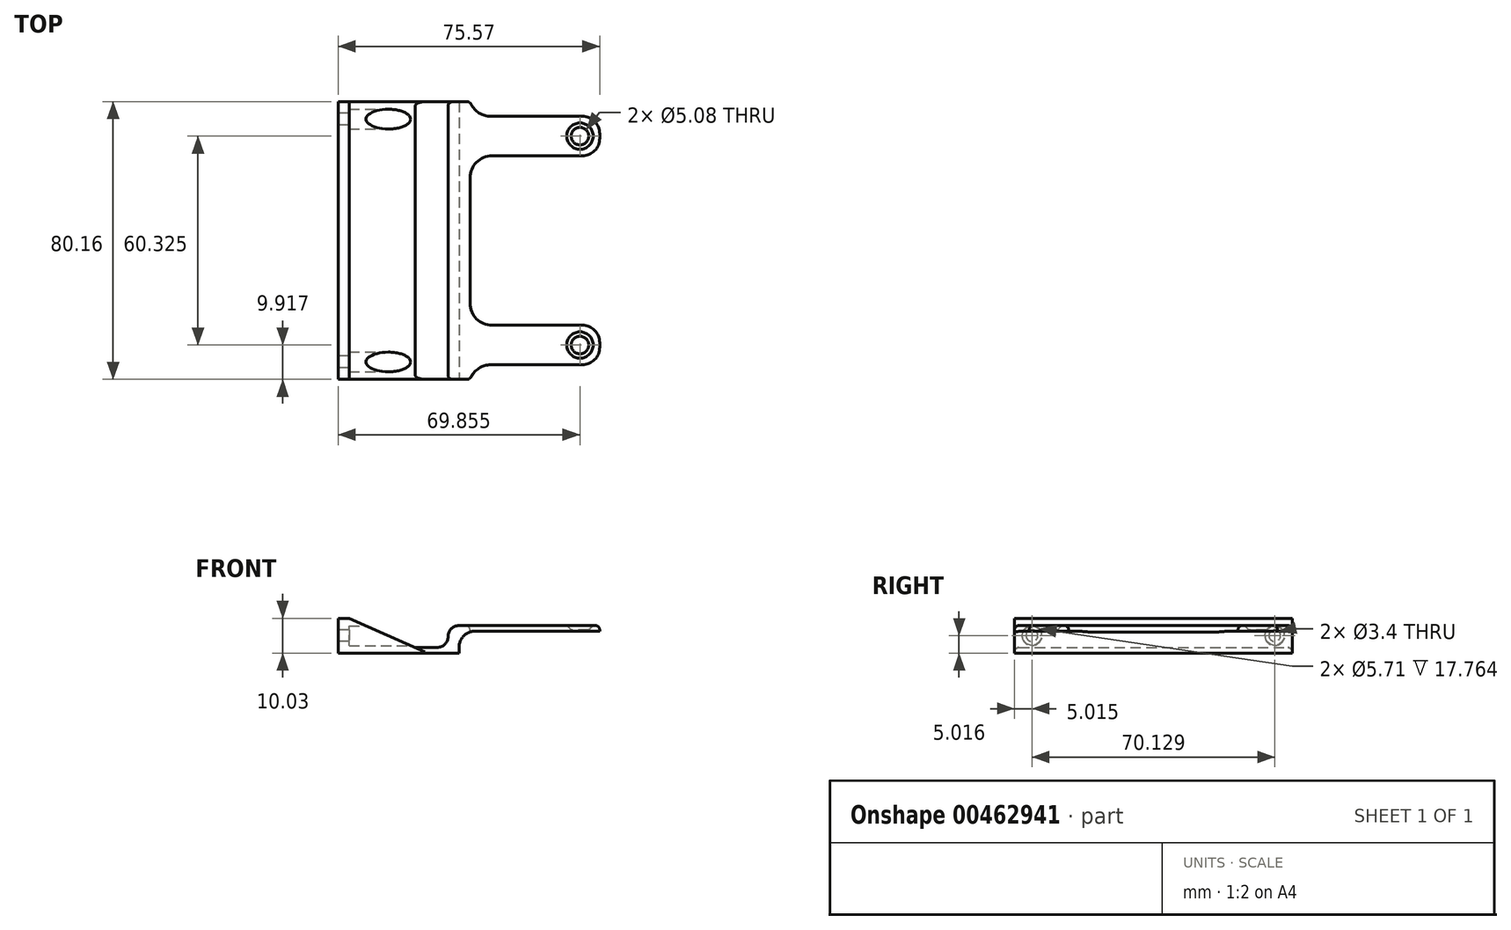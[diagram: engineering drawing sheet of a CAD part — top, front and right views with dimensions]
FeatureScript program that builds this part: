
annotation { "Feature Type Name" : "Feature", "Feature Type Description" : "" }
export const myFeature = defineFeature(function(context is Context, id is Id, definition is map)
    precondition{}
    {
        {
            var Q0;
            Q0=qCreatedBy(makeId("Top.planeOp"),FACE);
            var sketch = newSketch(context, id + "F0", { "sketchPlane" : qUnion([Q0])});
            skLineSegment(sketch, "E0.bottom", {"start": v(-34.93, 40.08) * mm, "end": v(0, 40.08) * mm});
            skLineSegment(sketch, "E0.top", {"start": v(-34.93, -40.08) * mm, "end": v(0, -40.08) * mm});
            skLineSegment(sketch, "E0.left", {"start": v(-34.93, 40.08) * mm, "end": v(-34.93, -40.08) * mm});
            skLineSegment(sketch, "E0.right", {"start": v(0, 40.08) * mm, "end": v(0, -40.08) * mm});
            skSolve(sketch);
        }
        {
            var Q0;
            Q0 = qSketchRegion(id + "F0", true);
            extrude(context, id + "F1", {"entities" : qUnion([Q0]), "depth" : 1.59 * mm});
        }
        {
            var Q0;
            Q0=qCreatedBy(makeId("Top.planeOp"),FACE);
            var sketch = newSketch(context, id + "F2", { "sketchPlane" : qUnion([Q0])});
            skLineSegment(sketch, "E1.bottom", {"start": v(0, 40.08) * mm, "end": v(-3.18, 40.08) * mm});
            skLineSegment(sketch, "E1.top", {"start": v(0, -40.08) * mm, "end": v(-3.17, -40.08) * mm});
            skLineSegment(sketch, "E1.left", {"start": v(0, 40.08) * mm, "end": v(0, -40.08) * mm});
            skLineSegment(sketch, "E1.right", {"start": v(-3.18, 40.08) * mm, "end": v(-3.17, -40.08) * mm});
            skSolve(sketch);
        }
        {
            var Q0;
            Q0 = qSketchRegion(id + "F2", true);
            extrude(context, id + "F3", {"entities" : qUnion([Q0]), "operationType" : NewBodyOperationType.ADD, "depth" : 6.35 * mm});
        }
        {
            var Q0;
            Q0=makeQuery(id+"F3.opExtrude","CAP_FACE",FACE,{"disambiguationData":[OSD([sQuery(id+"F2.wireOp",EDGE,"E1.bottom"),sQuery(id+"F2.wireOp",EDGE,"E1.top"),sQuery(id+"F2.wireOp",EDGE,"E1.left"),sQuery(id+"F2.wireOp",EDGE,"E1.right")])],"isStart":false});
            var sketch = newSketch(context, id + "F4", { "sketchPlane" : qUnion([Q0])});
            skLineSegment(sketch, "E2", {"start": v(0, 0) * mm, "end": v(-34.93, 0) * mm, "construction": true});
            skPoint(sketch, "E2.endSnap0", {"position": v(0, 0) * mm});
            skLineSegment(sketch, "E3.bottom", {"start": v(-3.18, 35.88) * mm, "end": v(40.64, 35.88) * mm});
            skLineSegment(sketch, "E3.top", {"start": v(-3.18, 24.45) * mm, "end": v(40.64, 24.45) * mm});
            skLineSegment(sketch, "E3.left", {"start": v(-3.18, 35.88) * mm, "end": v(-3.18, 24.45) * mm});
            skLineSegment(sketch, "E3.right", {"start": v(40.64, 35.88) * mm, "end": v(40.64, 24.45) * mm});
            skLineSegment(sketch, "E4", {"start": v(34.92, 35.88) * mm, "end": v(34.92, 30.16) * mm, "construction": true});
            skLineSegment(sketch, "E5", {"start": v(34.93, 30.16) * mm, "end": v(34.93, 24.45) * mm, "construction": true});
            skLineSegment(sketch, "E6", {"start": v(34.93, 30.16) * mm, "end": v(40.64, 30.16) * mm, "construction": true});
            skCircle(sketch, "E7", {"center": v(34.93, 30.16) * mm, "radius": 2.54 * mm});
            skLineSegment(sketch, "E8.MirrorCS", {"start": v(-3.18, -35.88) * mm, "end": v(40.64, -35.88) * mm});
            skLineSegment(sketch, "E9.MirrorCS", {"start": v(34.93, -30.16) * mm, "end": v(40.64, -30.16) * mm, "construction": true});
            skLineSegment(sketch, "E10.MirrorCS", {"start": v(-3.18, -24.45) * mm, "end": v(40.64, -24.45) * mm});
            skLineSegment(sketch, "E11.MirrorCS", {"start": v(-3.18, -35.88) * mm, "end": v(-3.18, -24.45) * mm});
            skCircle(sketch, "E12.MirrorC", {"center": v(34.93, -30.16) * mm, "radius": 2.54 * mm});
            skLineSegment(sketch, "E13.MirrorCS", {"start": v(40.64, -35.88) * mm, "end": v(40.64, -24.45) * mm});
            skLineSegment(sketch, "E14.MirrorCS", {"start": v(34.93, -30.16) * mm, "end": v(34.93, -24.45) * mm, "construction": true});
            skLineSegment(sketch, "E15.MirrorCS", {"start": v(34.93, -35.88) * mm, "end": v(34.93, -30.16) * mm, "construction": true});
            skSolve(sketch);
        }
        {
            var Q0;
            Q0 = qSketchRegion(id + "F4", true);
            extrude(context, id + "F5", {"entities" : qUnion([Q0]), "operationType" : NewBodyOperationType.ADD, "depth" : 1.59 * mm});
        }
        {
            var Q0;
            Q0=makeQuery(id+"F5.opExtrude","CAP_FACE",FACE,{"disambiguationData":[OSD([sQuery(id+"F4.wireOp",EDGE,"E3.bottom"),sQuery(id+"F4.wireOp",EDGE,"E3.top"),sQuery(id+"F4.wireOp",EDGE,"E3.left"),sQuery(id+"F4.wireOp",EDGE,"E3.right"),sQuery(id+"F4.wireOp",EDGE,"E7")])],"isStart":false});
            var sketch = newSketch(context, id + "F6", { "sketchPlane" : qUnion([Q0])});
            skLineSegment(sketch, "E16.bottom", {"start": v(-3.18, 40.08) * mm, "end": v(3.17, 40.08) * mm});
            skLineSegment(sketch, "E16.top", {"start": v(-3.17, -40.08) * mm, "end": v(3.17, -40.08) * mm});
            skLineSegment(sketch, "E16.left", {"start": v(-3.18, 40.08) * mm, "end": v(-3.18, -40.08) * mm});
            skLineSegment(sketch, "E16.right", {"start": v(3.17, 40.08) * mm, "end": v(3.17, -40.08) * mm});
            skSolve(sketch);
        }
        {
            var Q0;
            Q0 = qSketchRegion(id + "F6", true);
            var Q1;
            {var subQ1=sQuery(id+"F4.wireOp",EDGE,"E3.top");var subQ2=sQuery(id+"F2.wireOp",EDGE,"E1.right");var subQ4=sQuery(id+"F2.wireOp",EDGE,"E1.left");Q1=makeQuery(id+"F5.boolean.opBoolean","SPLIT",FACE,{"disambiguationData":[TD([makeQuery(id+"F5.opExtrude","SWEPT_FACE",FACE,{"disambiguationData":[OSD([subQ1])]})])],"derivedFrom":makeQuery(id+"F3.opExtrude","CAP_FACE",FACE,{"disambiguationData":[OSD([sQuery(id+"F2.wireOp",EDGE,"E1.bottom"),sQuery(id+"F2.wireOp",EDGE,"E1.top"),subQ4,subQ2])],"isStart":false})});}
            extrude(context, id + "F7", {"entities" : qUnion([Q0]), "operationType" : NewBodyOperationType.ADD, "endBound" : BoundingType.UP_TO_SURFACE, "oppositeDirection" : true, "endBoundEntityFace" : qUnion([Q1]), "depth" : 25.4 * mm});
        }
        {
            var Q0;
            Q0=makeQuery(id+"F5.opExtrude","SWEPT_EDGE",EDGE,{"disambiguationData":[OSD([sQuery(id+"F4.wireOp",EDGE,"E8.MirrorCS"),sQuery(id+"F4.wireOp",EDGE,"E13.MirrorCS")])]});
            var Q1;
            Q1=makeQuery(id+"F5.opExtrude","SWEPT_EDGE",EDGE,{"disambiguationData":[OSD([sQuery(id+"F4.wireOp",EDGE,"E10.MirrorCS"),sQuery(id+"F4.wireOp",EDGE,"E13.MirrorCS")])]});
            var Q2;
            Q2=makeQuery(id+"F5.opExtrude","SWEPT_EDGE",EDGE,{"disambiguationData":[OSD([sQuery(id+"F4.wireOp",EDGE,"E3.top"),sQuery(id+"F4.wireOp",EDGE,"E3.right")])]});
            var Q3;
            Q3=makeQuery(id+"F5.opExtrude","SWEPT_EDGE",EDGE,{"disambiguationData":[OSD([sQuery(id+"F4.wireOp",EDGE,"E3.bottom"),sQuery(id+"F4.wireOp",EDGE,"E3.right")])]});
            fillet(context, id + "F8", {"entities" : qUnion([Q0, Q1, Q2, Q3]), "radius" : 5.08 * mm, "tangentPropagation" : true, "allowEdgeOverflow" : false});
        }
        {
            var Q0;
            {var subQ0=sQuery(id+"F4.wireOp",EDGE,"E3.top");var subQ1=makeQuery(id+"F5.opExtrude","CAP_FACE",FACE,{"disambiguationData":[OSD([sQuery(id+"F4.wireOp",EDGE,"E3.bottom"),subQ0,sQuery(id+"F4.wireOp",EDGE,"E3.left"),sQuery(id+"F4.wireOp",EDGE,"E3.right"),sQuery(id+"F4.wireOp",EDGE,"E7")])],"isStart":true});var subQ2=sQuery(id+"F2.wireOp",EDGE,"E1.left");var subQ3=makeQuery(id+"F3.opExtrude","SWEPT_FACE",FACE,{"disambiguationData":[OSD([subQ2])]});var subQ4=makeQuery(id+"F1.opExtrude","SWEPT_FACE",FACE,{"disambiguationData":[OSD([sQuery(id+"F0.wireOp",EDGE,"E0.right")])]});var subQ5=sQuery(id+"F4.wireOp",EDGE,"E10.MirrorCS");var subQ6=makeQuery(id+"F3.opExtrude","CAP_FACE",FACE,{"disambiguationData":[OSD([sQuery(id+"F2.wireOp",EDGE,"E1.bottom"),sQuery(id+"F2.wireOp",EDGE,"E1.top"),subQ2,sQuery(id+"F2.wireOp",EDGE,"E1.right")])],"isStart":false});var subQ7=makeQuery(id+"F5.opExtrude","CAP_FACE",FACE,{"disambiguationData":[OSD([sQuery(id+"F4.wireOp",EDGE,"E8.MirrorCS"),subQ5,sQuery(id+"F4.wireOp",EDGE,"E11.MirrorCS"),sQuery(id+"F4.wireOp",EDGE,"E12.MirrorC"),sQuery(id+"F4.wireOp",EDGE,"E13.MirrorCS")])],"isStart":true});var subQ8=makeQuery(id+"F3.opExtrude","CAP_EDGE",EDGE,{"disambiguationData":[OSD([subQ2])],"isStart":false});Q0=makeQuery(id+"F7.boolean.opBoolean","MERGE",EDGE,{"derivedFrom":[makeQuery(id+"F5.boolean.opBoolean","SPLIT",EDGE,{"disambiguationData":[topologyDisambiguationEdgeConnected([subQ4,subQ3,subQ1])],"derivedFrom":subQ8}),makeQuery(id+"F5.boolean.opBoolean","SPLIT",EDGE,{"disambiguationData":[topologyDisambiguationEdgeConnected([subQ4,subQ3,subQ7])],"derivedFrom":subQ8}),makeQuery(id+"F5.boolean.opBoolean","SPLIT",EDGE,{"disambiguationData":[topologyDisambiguationEdgeConnected([subQ4,subQ6,subQ3]),TD([makeQuery(id+"F5.opExtrude","SWEPT_FACE",FACE,{"disambiguationData":[OSD([subQ0])]})])],"derivedFrom":subQ8})]});}
            fillet(context, id + "F9", {"entities" : qUnion([Q0]), "radius" : 4.76 * mm, "tangentPropagation" : true, "allowEdgeOverflow" : false});
        }
        {
            var Q0;
            Q0=makeQuery(id+"F5.opExtrude","CAP_EDGE",EDGE,{"disambiguationData":[OSD([sQuery(id+"F4.wireOp",EDGE,"E12.MirrorC")])],"isStart":false});
            var Q1;
            Q1=makeQuery(id+"F5.opExtrude","CAP_EDGE",EDGE,{"disambiguationData":[OSD([sQuery(id+"F4.wireOp",EDGE,"E7")])],"isStart":false});
            chamfer(context, id + "F10", {"entities" : qUnion([Q0, Q1]), "width" : 1.27 * mm, "tangentPropagation" : true});
        }
        {
            var Q0;
            Q0=makeQuery(id+"F1.opExtrude","SWEPT_FACE",FACE,{"disambiguationData":[OSD([sQuery(id+"F0.wireOp",EDGE,"E0.left")])]});
            var sketch = newSketch(context, id + "F11", { "sketchPlane" : qUnion([Q0])});
            skLineSegment(sketch, "E17.bottom", {"start": v(40.08, 0) * mm, "end": v(-40.08, 0) * mm});
            skLineSegment(sketch, "E17.top", {"start": v(40.08, 10.03) * mm, "end": v(-40.08, 10.03) * mm});
            skLineSegment(sketch, "E17.left", {"start": v(40.08, 0) * mm, "end": v(40.08, 10.03) * mm});
            skLineSegment(sketch, "E17.right", {"start": v(-40.08, 0) * mm, "end": v(-40.08, 10.03) * mm});
            skLineSegment(sketch, "E18", {"start": v(40.08, 5.02) * mm, "end": v(35.06, 5.02) * mm, "construction": true});
            skLineSegment(sketch, "E19", {"start": v(35.06, 5.02) * mm, "end": v(35.06, 10.03) * mm, "construction": true});
            skLineSegment(sketch, "E20", {"start": v(35.06, 5.02) * mm, "end": v(35.06, 0) * mm, "construction": true});
            skCircle(sketch, "E21", {"center": v(35.06, 5.02) * mm, "radius": 1.7 * mm});
            skCircle(sketch, "E22.MirrorC", {"center": v(-35.06, 5.02) * mm, "radius": 1.7 * mm});
            skLineSegment(sketch, "E23.MirrorCS", {"start": v(-35.06, 5.02) * mm, "end": v(-35.06, 0) * mm, "construction": true});
            skLineSegment(sketch, "E24.MirrorCS", {"start": v(-35.06, 5.02) * mm, "end": v(-35.06, 10.03) * mm, "construction": true});
            skLineSegment(sketch, "E25.MirrorCS", {"start": v(-40.08, 5.02) * mm, "end": v(-35.06, 5.02) * mm, "construction": true});
            skSolve(sketch);
        }
        {
            var Q0;
            Q0 = qSketchRegion(id + "F11", true);
            extrude(context, id + "F12", {"entities" : qUnion([Q0]), "operationType" : NewBodyOperationType.ADD, "oppositeDirection" : true, "depth" : 3.17 * mm});
        }
        {
            var Q0;
            Q0=makeQuery(id+"F12.boolean.opBoolean","MERGE",FACE,{"derivedFrom":[makeQuery(id+"F3.boolean.opBoolean","MERGE",FACE,{"derivedFrom":[makeQuery(id+"F1.opExtrude","SWEPT_FACE",FACE,{"disambiguationData":[OSD([sQuery(id+"F0.wireOp",EDGE,"E0.top")])]}),makeQuery(id+"F3.opExtrude","SWEPT_FACE",FACE,{"disambiguationData":[OSD([sQuery(id+"F2.wireOp",EDGE,"E1.top")])]})]}),makeQuery(id+"F12.opExtrude","SWEPT_FACE",FACE,{"disambiguationData":[OSD([sQuery(id+"F11.wireOp",EDGE,"E17.left")])]})]});
            var sketch = newSketch(context, id + "F13", { "sketchPlane" : qUnion([Q0])});
            skLineSegment(sketch, "E26", {"start": v(-31.75, 10.03) * mm, "end": v(-12.7, 1.59) * mm});
            skLineSegment(sketch, "E27", {"start": v(-12.7, 1.59) * mm, "end": v(-31.75, 1.59) * mm});
            skLineSegment(sketch, "E28", {"start": v(-31.75, 1.59) * mm, "end": v(-31.75, 10.03) * mm});
            skSolve(sketch);
        }
        {
            var Q0;
            Q0 = qSketchRegion(id + "F13", true);
            var Q1;
            Q1=makeQuery(id+"F12.boolean.opBoolean","MERGE",FACE,{"derivedFrom":[makeQuery(id+"F3.boolean.opBoolean","MERGE",FACE,{"derivedFrom":[makeQuery(id+"F1.opExtrude","SWEPT_FACE",FACE,{"disambiguationData":[OSD([sQuery(id+"F0.wireOp",EDGE,"E0.bottom")])]}),makeQuery(id+"F3.opExtrude","SWEPT_FACE",FACE,{"disambiguationData":[OSD([sQuery(id+"F2.wireOp",EDGE,"E1.bottom")])]})]}),makeQuery(id+"F12.opExtrude","SWEPT_FACE",FACE,{"disambiguationData":[OSD([sQuery(id+"F11.wireOp",EDGE,"E17.right")])]})]});
            extrude(context, id + "F14", {"entities" : qUnion([Q0]), "operationType" : NewBodyOperationType.ADD, "endBound" : BoundingType.UP_TO_SURFACE, "oppositeDirection" : true, "endBoundEntityFace" : qUnion([Q1]), "depth" : 25.4 * mm});
        }
        {
            var Q0;
            Q0=makeQuery(id+"F7.boolean.opBoolean","MERGE",FACE,{"derivedFrom":[makeQuery(id+"F5.boolean.opBoolean","MERGE",FACE,{"derivedFrom":[makeQuery(id+"F3.opExtrude","SWEPT_FACE",FACE,{"disambiguationData":[OSD([sQuery(id+"F2.wireOp",EDGE,"E1.right")])]}),makeQuery(id+"F5.opExtrude","SWEPT_FACE",FACE,{"disambiguationData":[OSD([sQuery(id+"F4.wireOp",EDGE,"E3.left")])]}),makeQuery(id+"F5.opExtrude","SWEPT_FACE",FACE,{"disambiguationData":[OSD([sQuery(id+"F4.wireOp",EDGE,"E11.MirrorCS")])]})]}),makeQuery(id+"F7.opExtrude","SWEPT_FACE",FACE,{"disambiguationData":[OSD([sQuery(id+"F6.wireOp",EDGE,"Z5N6MeDG-fAUR-fTd4-oVM4-TOmCoqm82sNm.left")])]})]});
            var sketch = newSketch(context, id + "F15", { "sketchPlane" : qUnion([Q0])});
            skCircle(sketch, "E29.0", {"center": v(-35.06, 5.02) * mm, "radius": 1.7 * mm, "construction": true});
            skCircle(sketch, "E29.1", {"center": v(35.06, 5.02) * mm, "radius": 1.7 * mm, "construction": true});
            skCircle(sketch, "E30", {"center": v(35.06, 5.02) * mm, "radius": 2.86 * mm});
            skCircle(sketch, "E31", {"center": v(-35.06, 5.02) * mm, "radius": 2.86 * mm});
            skSolve(sketch);
        }
        {
            var Q0;
            Q0 = qSketchRegion(id + "F15", true);
            var Q1;
            {var subQ0=sQuery(id+"F11.wireOp",EDGE,"E17.left");var subQ1=sQuery(id+"F11.wireOp",EDGE,"E17.top");Q1=makeQuery(id+"F14.boolean.opBoolean","MERGE",VERTEX,{"derivedFrom":[makeQuery(id+"F12.opExtrude","CAP_VERTEX",VERTEX,{"disambiguationData":[OSD([subQ1,subQ0])],"isStart":false}),makeQuery(id+"F14.opExtrude","CAP_VERTEX",VERTEX,{"disambiguationData":[OSD([subQ1,subQ0,sQuery(id+"F13.wireOp",EDGE,"E26"),sQuery(id+"F13.wireOp",EDGE,"E28")])],"isStart":true})]});}
            extrude(context, id + "F16", {"entities" : qUnion([Q0]), "operationType" : NewBodyOperationType.REMOVE, "endBound" : BoundingType.UP_TO_VERTEX, "endBoundEntityVertex" : qUnion([Q1]), "depth" : 25.4 * mm});
        }
        {
            var Q0;
            Q0=makeQuery(id+"F3.boolean.opBoolean","INTERSECT",EDGE,{"derivedFrom":[makeQuery(id+"F1.opExtrude","CAP_FACE",FACE,{"disambiguationData":[OSD([sQuery(id+"F0.wireOp",EDGE,"E0.bottom"),sQuery(id+"F0.wireOp",EDGE,"E0.top"),sQuery(id+"F0.wireOp",EDGE,"E0.left"),sQuery(id+"F0.wireOp",EDGE,"E0.right")])],"isStart":false}),makeQuery(id+"F3.opExtrude","SWEPT_FACE",FACE,{"disambiguationData":[OSD([sQuery(id+"F2.wireOp",EDGE,"E1.right")])]})]});
            var Q1;
            Q1=makeQuery(id+"F7.boolean.opBoolean","MERGE",EDGE,{"derivedFrom":[makeQuery(id+"F5.opExtrude","CAP_EDGE",EDGE,{"disambiguationData":[OSD([sQuery(id+"F4.wireOp",EDGE,"E3.left")])],"isStart":false}),makeQuery(id+"F5.opExtrude","CAP_EDGE",EDGE,{"disambiguationData":[OSD([sQuery(id+"F4.wireOp",EDGE,"E11.MirrorCS")])],"isStart":false}),makeQuery(id+"F7.opExtrude","CAP_EDGE",EDGE,{"disambiguationData":[OSD([sQuery(id+"F6.wireOp",EDGE,"E16.left")])],"isStart":true})]});
            fillet(context, id + "F17", {"entities" : qUnion([Q0, Q1]), "radius" : 3.17 * mm, "tangentPropagation" : true, "allowEdgeOverflow" : false});
        }
        {
            var Q0;
            Q0=makeQuery(id+"F7.boolean.opBoolean","INTERSECT",EDGE,{"derivedFrom":[makeQuery(id+"F5.opExtrude","SWEPT_FACE",FACE,{"disambiguationData":[OSD([sQuery(id+"F4.wireOp",EDGE,"E8.MirrorCS")])]}),makeQuery(id+"F7.opExtrude","SWEPT_FACE",FACE,{"disambiguationData":[OSD([sQuery(id+"F6.wireOp",EDGE,"E16.right")])]})]});
            var Q1;
            Q1=makeQuery(id+"F7.boolean.opBoolean","INTERSECT",EDGE,{"derivedFrom":[makeQuery(id+"F5.opExtrude","SWEPT_FACE",FACE,{"disambiguationData":[OSD([sQuery(id+"F4.wireOp",EDGE,"E10.MirrorCS")])]}),makeQuery(id+"F7.opExtrude","SWEPT_FACE",FACE,{"disambiguationData":[OSD([sQuery(id+"F6.wireOp",EDGE,"E16.right")])]})]});
            var Q2;
            Q2=makeQuery(id+"F7.boolean.opBoolean","INTERSECT",EDGE,{"derivedFrom":[makeQuery(id+"F5.opExtrude","SWEPT_FACE",FACE,{"disambiguationData":[OSD([sQuery(id+"F4.wireOp",EDGE,"E3.bottom")])]}),makeQuery(id+"F7.opExtrude","SWEPT_FACE",FACE,{"disambiguationData":[OSD([sQuery(id+"F6.wireOp",EDGE,"E16.right")])]})]});
            var Q3;
            Q3=makeQuery(id+"F7.boolean.opBoolean","INTERSECT",EDGE,{"derivedFrom":[makeQuery(id+"F5.opExtrude","SWEPT_FACE",FACE,{"disambiguationData":[OSD([sQuery(id+"F4.wireOp",EDGE,"E3.top")])]}),makeQuery(id+"F7.opExtrude","SWEPT_FACE",FACE,{"disambiguationData":[OSD([sQuery(id+"F6.wireOp",EDGE,"E16.right")])]})]});
            fillet(context, id + "F18", {"entities" : qUnion([Q0, Q1, Q2, Q3]), "radius" : 6.35 * mm, "tangentPropagation" : true, "allowEdgeOverflow" : false});
        }
        {
            var Q0;
            Q0=makeQuery(id+"F18.opFillet","BLEND_EDGE",EDGE,{"blendedFrom":[makeQuery(id+"F7.boolean.opBoolean","INTERSECT",EDGE,{"derivedFrom":[makeQuery(id+"F5.opExtrude","SWEPT_FACE",FACE,{"disambiguationData":[OSD([sQuery(id+"F4.wireOp",EDGE,"E8.MirrorCS")])]}),makeQuery(id+"F7.opExtrude","SWEPT_FACE",FACE,{"disambiguationData":[OSD([sQuery(id+"F6.wireOp",EDGE,"E16.right")])]})]}),makeQuery(id+"F14.boolean.opBoolean","MERGE",FACE,{"derivedFrom":[makeQuery(id+"F12.boolean.opBoolean","MERGE",FACE,{"derivedFrom":[makeQuery(id+"F7.boolean.opBoolean","MERGE",FACE,{"derivedFrom":[makeQuery(id+"F3.boolean.opBoolean","MERGE",FACE,{"derivedFrom":[makeQuery(id+"F1.opExtrude","SWEPT_FACE",FACE,{"disambiguationData":[OSD([sQuery(id+"F0.wireOp",EDGE,"E0.top")])]}),makeQuery(id+"F3.opExtrude","SWEPT_FACE",FACE,{"disambiguationData":[OSD([sQuery(id+"F2.wireOp",EDGE,"E1.top")])]})]}),makeQuery(id+"F7.opExtrude","SWEPT_FACE",FACE,{"disambiguationData":[OSD([sQuery(id+"F6.wireOp",EDGE,"E16.top")])]})]}),makeQuery(id+"F12.opExtrude","SWEPT_FACE",FACE,{"disambiguationData":[OSD([sQuery(id+"F11.wireOp",EDGE,"E17.left")])]})]}),makeQuery(id+"F14.opExtrude","CAP_FACE",FACE,{"disambiguationData":[OSD([sQuery(id+"F13.wireOp",EDGE,"E26"),sQuery(id+"F13.wireOp",EDGE,"E27"),sQuery(id+"F13.wireOp",EDGE,"E28")])],"isStart":true})]})],"blendedInto":[makeQuery(id+"F14.boolean.opBoolean","MERGE",FACE,{"derivedFrom":[makeQuery(id+"F12.boolean.opBoolean","MERGE",FACE,{"derivedFrom":[makeQuery(id+"F7.boolean.opBoolean","MERGE",FACE,{"derivedFrom":[makeQuery(id+"F3.boolean.opBoolean","MERGE",FACE,{"derivedFrom":[makeQuery(id+"F1.opExtrude","SWEPT_FACE",FACE,{"disambiguationData":[OSD([sQuery(id+"F0.wireOp",EDGE,"E0.top")])]}),makeQuery(id+"F3.opExtrude","SWEPT_FACE",FACE,{"disambiguationData":[OSD([sQuery(id+"F2.wireOp",EDGE,"E1.top")])]})]}),makeQuery(id+"F7.opExtrude","SWEPT_FACE",FACE,{"disambiguationData":[OSD([sQuery(id+"F6.wireOp",EDGE,"E16.top")])]})]}),makeQuery(id+"F12.opExtrude","SWEPT_FACE",FACE,{"disambiguationData":[OSD([sQuery(id+"F11.wireOp",EDGE,"E17.left")])]})]}),makeQuery(id+"F14.opExtrude","CAP_FACE",FACE,{"disambiguationData":[OSD([sQuery(id+"F13.wireOp",EDGE,"E26"),sQuery(id+"F13.wireOp",EDGE,"E27"),sQuery(id+"F13.wireOp",EDGE,"E28")])],"isStart":true})]})]});
            var Q1;
            {var subQ0=sQuery(id+"F11.wireOp",EDGE,"E17.right");var subQ1=sQuery(id+"F6.wireOp",EDGE,"E16.bottom");var subQ2=sQuery(id+"F2.wireOp",EDGE,"E1.bottom");var subQ3=sQuery(id+"F0.wireOp",EDGE,"E0.bottom");Q1=makeQuery(id+"F18.opFillet","BLEND_EDGE",EDGE,{"blendedFrom":[makeQuery(id+"F7.boolean.opBoolean","INTERSECT",EDGE,{"derivedFrom":[makeQuery(id+"F5.opExtrude","SWEPT_FACE",FACE,{"disambiguationData":[OSD([sQuery(id+"F4.wireOp",EDGE,"E3.bottom")])]}),makeQuery(id+"F7.opExtrude","SWEPT_FACE",FACE,{"disambiguationData":[OSD([sQuery(id+"F6.wireOp",EDGE,"E16.right")])]})]}),makeQuery(id+"F14.boolean.opBoolean","MERGE",FACE,{"derivedFrom":[makeQuery(id+"F12.boolean.opBoolean","MERGE",FACE,{"derivedFrom":[makeQuery(id+"F7.boolean.opBoolean","MERGE",FACE,{"derivedFrom":[makeQuery(id+"F3.boolean.opBoolean","MERGE",FACE,{"derivedFrom":[makeQuery(id+"F1.opExtrude","SWEPT_FACE",FACE,{"disambiguationData":[OSD([subQ3])]}),makeQuery(id+"F3.opExtrude","SWEPT_FACE",FACE,{"disambiguationData":[OSD([subQ2])]})]}),makeQuery(id+"F7.opExtrude","SWEPT_FACE",FACE,{"disambiguationData":[OSD([subQ1])]})]}),makeQuery(id+"F12.opExtrude","SWEPT_FACE",FACE,{"disambiguationData":[OSD([subQ0])]})]}),makeQuery(id+"F14.opExtrude","CAP_FACE",FACE,{"disambiguationData":[OSD([subQ3,subQ2,subQ1,subQ0])],"isStart":false})]})],"blendedInto":[makeQuery(id+"F14.boolean.opBoolean","MERGE",FACE,{"derivedFrom":[makeQuery(id+"F12.boolean.opBoolean","MERGE",FACE,{"derivedFrom":[makeQuery(id+"F7.boolean.opBoolean","MERGE",FACE,{"derivedFrom":[makeQuery(id+"F3.boolean.opBoolean","MERGE",FACE,{"derivedFrom":[makeQuery(id+"F1.opExtrude","SWEPT_FACE",FACE,{"disambiguationData":[OSD([subQ3])]}),makeQuery(id+"F3.opExtrude","SWEPT_FACE",FACE,{"disambiguationData":[OSD([subQ2])]})]}),makeQuery(id+"F7.opExtrude","SWEPT_FACE",FACE,{"disambiguationData":[OSD([subQ1])]})]}),makeQuery(id+"F12.opExtrude","SWEPT_FACE",FACE,{"disambiguationData":[OSD([subQ0])]})]}),makeQuery(id+"F14.opExtrude","CAP_FACE",FACE,{"disambiguationData":[OSD([subQ3,subQ2,subQ1,subQ0])],"isStart":false})]})]});}
            fillet(context, id + "F19", {"entities" : qUnion([Q0, Q1]), "radius" : 1.27 * mm, "tangentPropagation" : true, "allowEdgeOverflow" : false});
        }
        {
            var Q0;
            Q0=makeQuery(id+"F5.opExtrude","CAP_EDGE",EDGE,{"disambiguationData":[OSD([sQuery(id+"F4.wireOp",EDGE,"E3.bottom")])],"isStart":false});
            fillet(context, id + "F20", {"entities" : qUnion([Q0]), "radius" : 1.27 * mm, "tangentPropagation" : true, "allowEdgeOverflow" : false});
        }
    });
